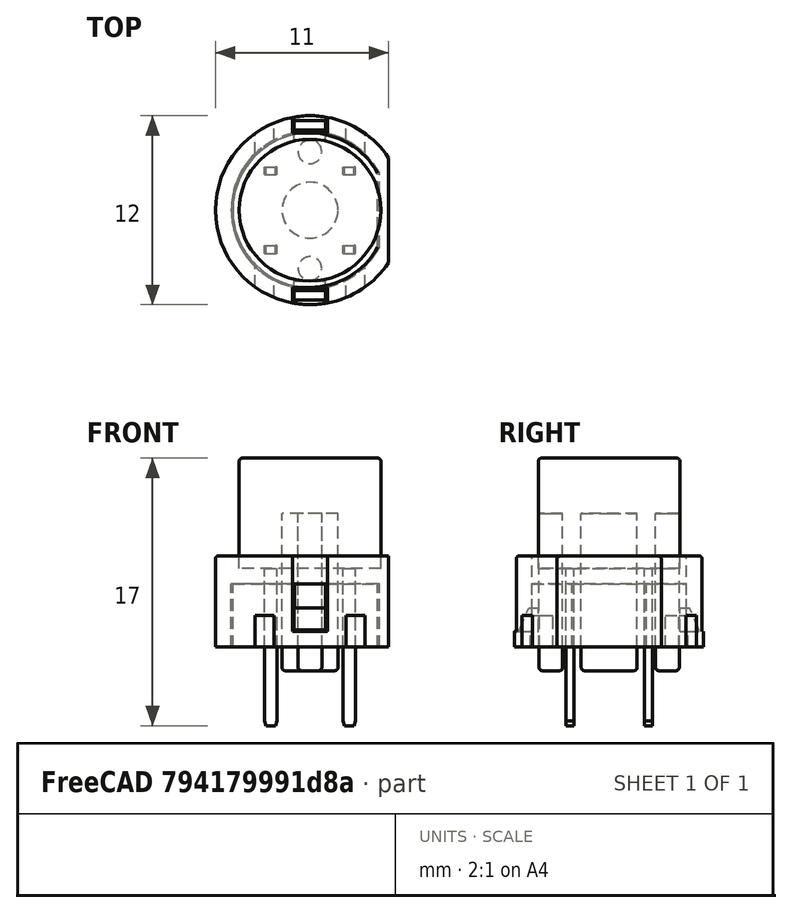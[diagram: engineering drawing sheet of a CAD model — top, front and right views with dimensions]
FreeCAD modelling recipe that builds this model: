
FCSTD DOCUMENT  (FreeCAD 0.18.4R)
Label: KS01-BV-GREY
License: All rights reserved
LicenseURL: http://en.wikipedia.org/wiki/All_rights_reserved
objects: Part::Box×13, Part::Cut×8, Part::Cylinder×7, Part::Fillet×6, Part::Chamfer×6
note: 40 computed .brp shape members not serialized (recipe doc carries the construction recipe); baked Part::Feature solids carry a one-line shape summary decoded from their .brp

FEATURE [Part::Cylinder] Cylinder
  Angle = 360
  AttacherType = Attacher::AttachEngine3D
  Height = 7
  Placement = pos=(0,0,5) rot=(0,0,1;0rad)
  Radius = 4.5
FEATURE [Part::Cylinder] Cylinder001
  Angle = 360
  AttacherType = Attacher::AttachEngine3D
  Height = 5.8
  Radius = 6
FEATURE [Part::Box] Box  label="Cube"
  AttacherType = Attacher::AttachEngine3D
  Height = 6
  Length = 1
  Placement = pos=(5,-6,0) rot=(0,0,1;0rad)
  Width = 12
FEATURE [Part::Cut] Cut
  Base = -> Cylinder001
  Tool = -> Box
FEATURE [Part::Cylinder] Cylinder002
  Angle = 360
  AttacherType = Attacher::AttachEngine3D
  Height = 10
  Placement = pos=(0,0,-1.5) rot=(0,0,1;0rad)
  Radius = 1.775
FEATURE [Part::Cylinder] Cylinder003
  Angle = 360
  AttacherType = Attacher::AttachEngine3D
  Height = 10
  Placement = pos=(0,3.7,-1.5) rot=(0,0,1;0rad)
  Radius = 0.75
FEATURE [Part::Cylinder] Cylinder004
  Angle = 360
  AttacherType = Attacher::AttachEngine3D
  Height = 10
  Placement = pos=(0,-3.7,-1.5) rot=(0,0,1;0rad)
  Radius = 0.75
FEATURE [Part::Fillet] Fillet
  Base = -> Cylinder004
  Edges = 1 edges r=0.2: [Edge3]
FEATURE [Part::Box] Box001  label="Cube001"
  AttacherType = Attacher::AttachEngine3D
  Height = 5
  Length = 1
  Placement = pos=(4.4,-6,0) rot=(0,0,1;0rad)
  Width = 12
FEATURE [Part::Cylinder] Cylinder005
  Angle = 360
  AttacherType = Attacher::AttachEngine3D
  Height = 4
  Radius = 5
FEATURE [Part::Cut] Cut001
  Base = -> Cylinder005
  Tool = -> Box001
FEATURE [Part::Cut] Cut002
  Base = -> Cut
  Tool = -> Cut001
FEATURE [Part::Box] Box002  label="Cube002"
  AttacherType = Attacher::AttachEngine3D
  Height = 5
  Length = 1
  Placement = pos=(4.3,-6,0) rot=(0,0,1;0rad)
  Width = 12
FEATURE [Part::Cylinder] Cylinder006
  Angle = 360
  AttacherType = Attacher::AttachEngine3D
  Height = 4
  Radius = 4.9
FEATURE [Part::Cut] Cut003
  Base = -> Cylinder006
  Tool = -> Box002
FEATURE [Part::Fillet] Fillet002
  Base = -> Cylinder002
  Edges = 1 edges r=0.2: [Edge3]
FEATURE [Part::Fillet] Fillet003
  Base = -> Cylinder003
  Edges = 1 edges r=0.2: [Edge3]
FEATURE [Part::Box] Box003  label="Cube003"
  AttacherType = Attacher::AttachEngine3D
  Height = 2
  Length = 1.2
  Placement = pos=(2.3,-6,0) rot=(0,0,1;0rad)
  Width = 12
FEATURE [Part::Box] Box004  label="Cube004"
  AttacherType = Attacher::AttachEngine3D
  Height = 2
  Length = 1.2
  Placement = pos=(-3.5,-6,0) rot=(0,0,1;0rad)
  Width = 12
FEATURE [Part::Cut] Cut004
  Base = -> Cut002
  Tool = -> Box003
FEATURE [Part::Cut] Cut005
  Base = -> Cut004
  Tool = -> Box004
FEATURE [Part::Box] Box005  label="Cube005"
  AttacherType = Attacher::AttachEngine3D
  Height = 5
  Length = 2.2
  Placement = pos=(-1.1,-7.9,1) rot=(0,0,1;0rad)
  Width = 3
FEATURE [Part::Box] Box006  label="Cube006"
  AttacherType = Attacher::AttachEngine3D
  Height = 5
  Length = 2.2
  Placement = pos=(-1.1,4.9,1) rot=(0,0,1;0rad)
  Width = 3
FEATURE [Part::Cut] Cut006
  Base = -> Cut005
  Tool = -> Box005
FEATURE [Part::Cut] Cut007
  Base = -> Cut006
  Tool = -> Box006
FEATURE [Part::Fillet] Fillet004
  Base = -> Cylinder
  Edges = 1 edges r=0.2: [Edge1]
FEATURE [Part::Fillet] Fillet005
  Base = -> Cut007
  Edges = 2 edges r=0.2: [Edge1,Edge5]
FEATURE [Part::Fillet] Fillet006
  Base = -> Fillet005
  Edges = 1 edges r=0.2: [Edge15]
FEATURE [Part::Box] Box007  label="Cube007"
  AttacherType = Attacher::AttachEngine3D
  Height = 10
  Length = 0.8
  Placement = pos=(0,0,-5) rot=(0,0,1;0rad)
  Width = 0.5
FEATURE [Part::Chamfer] Chamfer  label="Chamfer000"
  Base = -> Box007
  Edges = 2 edges: [Edge4 r1=0.3 r2=0.1,Edge8 r1=0.3 r2=0.1]
  Placement = pos=(-2.9,2.25,0) rot=(0,0,1;0rad)
FEATURE [Part::Box] Box008  label="Cube008"
  AttacherType = Attacher::AttachEngine3D
  Height = 10
  Length = 0.8
  Placement = pos=(0,0,-5) rot=(0,0,1;0rad)
  Width = 0.5
FEATURE [Part::Chamfer] Chamfer001
  Base = -> Box008
  Edges = 2 edges: [Edge4 r1=0.3 r2=0.1,Edge8 r1=0.3 r2=0.1]
  Placement = pos=(-2.9,-2.75,0) rot=(0,0,1;0rad)
FEATURE [Part::Box] Box009  label="Cube009"
  AttacherType = Attacher::AttachEngine3D
  Height = 10
  Length = 0.8
  Placement = pos=(0,0,-5) rot=(0,0,1;0rad)
  Width = 0.5
FEATURE [Part::Chamfer] Chamfer002
  Base = -> Box009
  Edges = 2 edges: [Edge4 r1=0.3 r2=0.1,Edge8 r1=0.3 r2=0.1]
  Placement = pos=(2.1,-2.75,0) rot=(0,0,1;0rad)
FEATURE [Part::Box] Box010  label="Cube010"
  AttacherType = Attacher::AttachEngine3D
  Height = 10
  Length = 0.8
  Placement = pos=(0,0,-5) rot=(0,0,1;0rad)
  Width = 0.5
FEATURE [Part::Chamfer] Chamfer003
  Base = -> Box010
  Edges = 2 edges: [Edge4 r1=0.3 r2=0.1,Edge8 r1=0.3 r2=0.1]
  Placement = pos=(2.1,2.25,0) rot=(0,0,1;0rad)
FEATURE [Part::Box] Box012  label="Cube012"
  AttacherType = Attacher::AttachEngine3D
  Height = 1.5
  Length = 2
  Placement = pos=(-1,-5.7,1) rot=(0,0,1;0rad)
  Width = 1.2
FEATURE [Part::Chamfer] Chamfer005
  Base = -> Box012
  Edges = 1 edges: [Edge10 r1=1.4 r2=0.6]
FEATURE [Part::Box] Box013  label="Cube013"
  AttacherType = Attacher::AttachEngine3D
  Height = 1.5
  Length = 2
  Placement = pos=(-1,4.5,1) rot=(0,0,1;0rad)
  Width = 1.2
FEATURE [Part::Chamfer] Chamfer006
  Base = -> Box013
  Edges = 1 edges: [Edge12 r1=1.4 r2=0.6]
